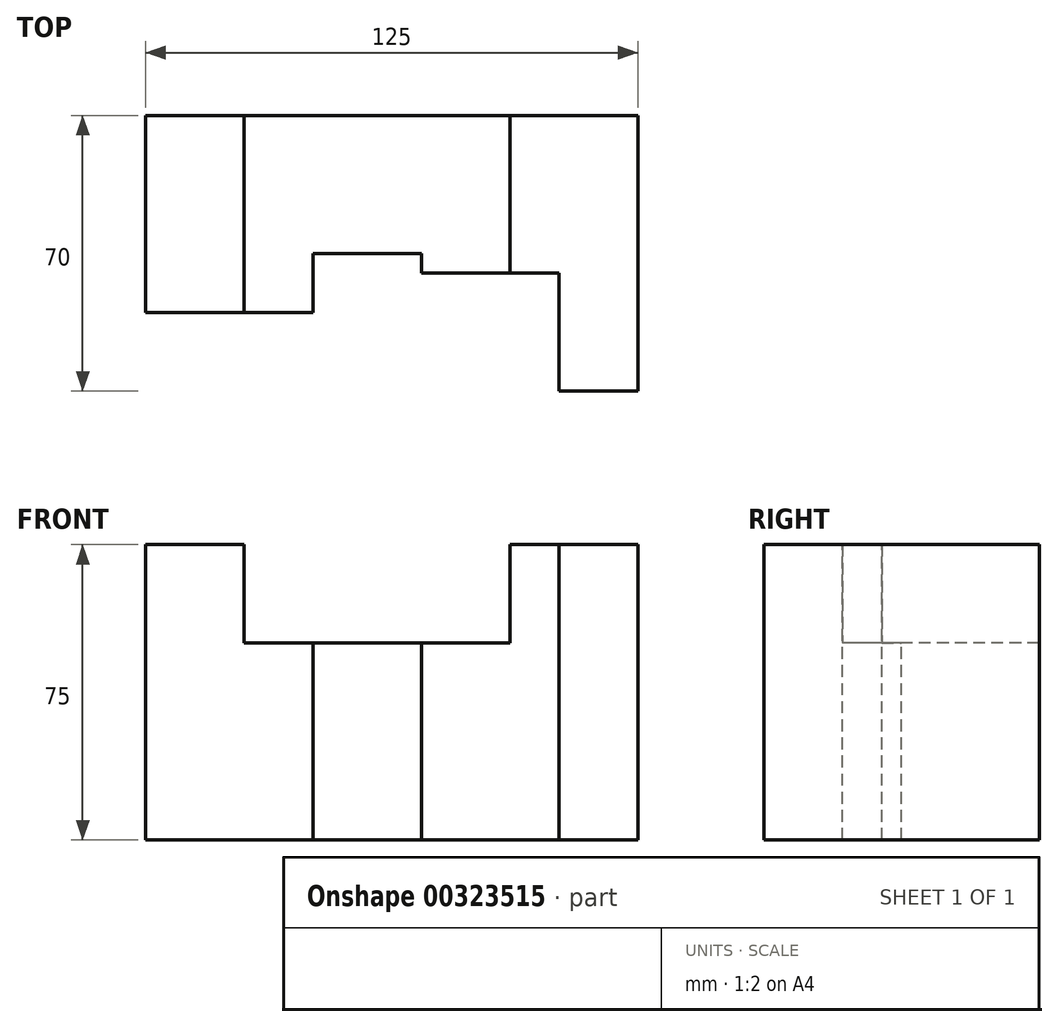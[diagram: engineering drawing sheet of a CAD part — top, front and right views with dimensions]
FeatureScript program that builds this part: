
annotation { "Feature Type Name" : "Feature", "Feature Type Description" : "" }
export const myFeature = defineFeature(function(context is Context, id is Id, definition is map)
    precondition{}
    {
        {
            var Q0;
            Q0=qCreatedBy(makeId("Top.planeOp"),FACE);
            var sketch = newSketch(context, id + "F0", { "sketchPlane" : qUnion([Q0])});
            skLineSegment(sketch, "E0", {"start": v(-32.92, 37.12) * mm, "end": v(-7.92, 37.12) * mm});
            skLineSegment(sketch, "E1", {"start": v(-7.92, 37.12) * mm, "end": v(62.08, 37.12) * mm});
            skLineSegment(sketch, "E2", {"start": v(62.08, 37.12) * mm, "end": v(92.08, 37.12) * mm});
            skLineSegment(sketch, "E3", {"start": v(92.08, 37.12) * mm, "end": v(92.08, -32.88) * mm});
            skLineSegment(sketch, "E4", {"start": v(92.08, -32.88) * mm, "end": v(72.08, -32.88) * mm});
            skLineSegment(sketch, "E5", {"start": v(72.08, -32.88) * mm, "end": v(72.08, -2.88) * mm});
            skLineSegment(sketch, "E6", {"start": v(72.08, -2.88) * mm, "end": v(62.08, -2.88) * mm});
            skLineSegment(sketch, "E7", {"start": v(62.08, -2.88) * mm, "end": v(37.08, -2.88) * mm});
            skLineSegment(sketch, "E8", {"start": v(37.08, -2.88) * mm, "end": v(37.08, 2.12) * mm});
            skLineSegment(sketch, "E9", {"start": v(37.08, 2.12) * mm, "end": v(9.58, 2.12) * mm});
            skLineSegment(sketch, "E10", {"start": v(9.58, 2.12) * mm, "end": v(9.58, -12.88) * mm});
            skLineSegment(sketch, "E11", {"start": v(9.58, -12.88) * mm, "end": v(-7.92, -12.88) * mm});
            skLineSegment(sketch, "E12", {"start": v(-7.92, -12.88) * mm, "end": v(-32.92, -12.88) * mm});
            skLineSegment(sketch, "E13", {"start": v(-32.92, -12.88) * mm, "end": v(-32.92, 37.12) * mm});
            skLineSegment(sketch, "E14", {"start": v(-7.92, 37.12) * mm, "end": v(-7.92, -12.88) * mm});
            skLineSegment(sketch, "E15", {"start": v(62.08, 37.12) * mm, "end": v(62.08, -2.88) * mm});
            skSolve(sketch);
        }
        {
            var Q0;
            Q0=makeQuery(id+"F0.imprint","IMPRINT",FACE,{"disambiguationData":[TD([[makeQuery(id+"F0.imprint","IMPRINT",EDGE,{"derivedFrom":sQuery(id+"F0.wireOp",EDGE,"E0")}),-1.0]])]});
            var Q1;
            Q1=makeQuery(id+"F0.imprint","IMPRINT",FACE,{"disambiguationData":[TD([[makeQuery(id+"F0.imprint","IMPRINT",EDGE,{"derivedFrom":sQuery(id+"F0.wireOp",EDGE,"E1")}),-1.0]])]});
            var Q2;
            Q2=makeQuery(id+"F0.imprint","IMPRINT",FACE,{"disambiguationData":[TD([[makeQuery(id+"F0.imprint","IMPRINT",EDGE,{"derivedFrom":sQuery(id+"F0.wireOp",EDGE,"E2")}),-1.0]])]});
            extrude(context, id + "F1", {"entities" : qUnion([Q0, Q1, Q2]), "oppositeDirection" : true, "depth" : 75 * mm});
        }
        {
            var Q0;
            Q0=makeQuery(id+"F1.opExtrude","SWEPT_FACE",FACE,{"disambiguationData":[OSD([sQuery(id+"F0.wireOp",EDGE,"E11"),sQuery(id+"F0.wireOp",EDGE,"E12")])]});
            var sketch = newSketch(context, id + "F2", { "sketchPlane" : qUnion([Q0])});
            skLineSegment(sketch, "E16", {"start": v(9.58, -25) * mm, "end": v(59.58, -25) * mm});
            skLineSegment(sketch, "E17", {"start": v(9.58, 0) * mm, "end": v(-7.92, 0) * mm});
            skLineSegment(sketch, "E18", {"start": v(-7.92, 0) * mm, "end": v(-7.92, -25) * mm});
            skLineSegment(sketch, "E19", {"start": v(-7.92, -25) * mm, "end": v(9.58, -25) * mm});
            skLineSegment(sketch, "E20", {"start": v(59.58, -25) * mm, "end": v(59.58, 0) * mm});
            skLineSegment(sketch, "E21", {"start": v(59.58, 0) * mm, "end": v(9.58, 0) * mm});
            skSolve(sketch);
        }
        {
            var Q0;
            Q0 = qSketchRegion(id + "F2", true);
            extrude(context, id + "F3", {"entities" : qUnion([Q0]), "operationType" : NewBodyOperationType.REMOVE, "oppositeDirection" : true, "depth" : 70 * mm});
        }
    });
